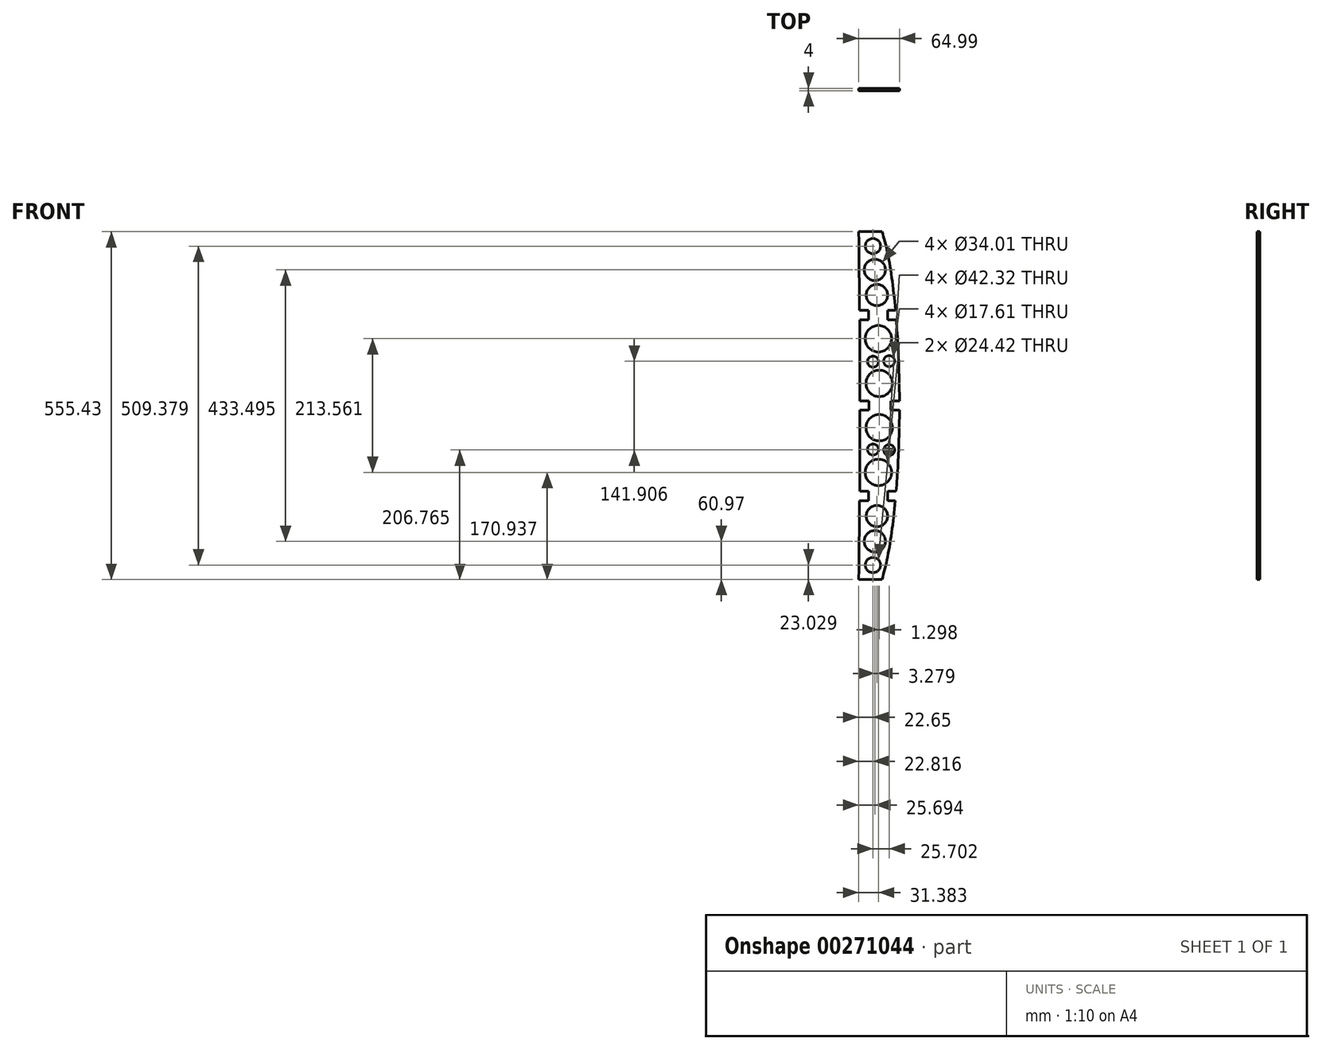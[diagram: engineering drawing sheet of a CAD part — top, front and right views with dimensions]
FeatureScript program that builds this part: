
annotation { "Feature Type Name" : "Feature", "Feature Type Description" : "" }
export const myFeature = defineFeature(function(context is Context, id is Id, definition is map)
    precondition{}
    {
        {
            var Q0;
            Q0=qCreatedBy(makeId("Front.planeOp"),FACE);
            var sketch = newSketch(context, id + "F0", { "sketchPlane" : qUnion([Q0])});
            skLineSegment(sketch, "E0", {"start": v(-136.03, -529.8) * mm, "end": v(-201.03, -530.28) * mm});
            skLineSegment(sketch, "E1", {"start": v(-201.03, -530.28) * mm, "end": v(-201.03, -252.28) * mm});
            skLineSegment(sketch, "E2", {"start": v(-201.03, -252.28) * mm, "end": v(-164.03, -252.28) * mm});
            skLineSegment(sketch, "E3.MirrorCS", {"start": v(-201.03, -530.28) * mm, "end": v(-196.95, -808.25) * mm});
            skLineSegment(sketch, "E4.MirrorCS", {"start": v(-196.95, -808.25) * mm, "end": v(-159.95, -807.7) * mm});
            skFitSpline(sketch, "E5", {"points": [v(-164.03, -252.28) * mm, v(-136.03, -529.8) * mm, v(-159.95, -807.7) * mm], "startDerivative": vector(123.85, -382.51) * mm, "endDerivative": vector(-100.33, -397.76) * mm});
            skLineSegment(sketch, "E6", {"start": v(-201.03, -530.28) * mm, "end": v(-199.03, -530.27) * mm});
            skFitSpline(sketch, "E7", {"points": [v(-201.03, -252.28) * mm, v(-199.03, -530.27) * mm, v(-196.95, -808.25) * mm], "startDerivative": vector(9.34, -915.38) * mm, "endDerivative": vector(6.18, -771.13) * mm});
            skLineSegment(sketch, "E8", {"start": v(-188.97, -530.2) * mm, "end": v(-189.03, -522.7) * mm});
            skLineSegment(sketch, "E9", {"start": v(-189.03, -522.7) * mm, "end": v(-201.03, -522.78) * mm});
            skLineSegment(sketch, "E10", {"start": v(-150.04, -529.9) * mm, "end": v(-150.04, -522.7) * mm});
            skLineSegment(sketch, "E11", {"start": v(-150.04, -522.7) * mm, "end": v(-136.04, -522.6) * mm});
            skLineSegment(sketch, "E12.MirrorCS", {"start": v(-149.94, -537.12) * mm, "end": v(-135.94, -537.02) * mm});
            skLineSegment(sketch, "E13.MirrorCS", {"start": v(-188.92, -537.7) * mm, "end": v(-200.92, -537.78) * mm});
            skLineSegment(sketch, "E14.MirrorCS", {"start": v(-150.04, -529.9) * mm, "end": v(-149.94, -537.12) * mm});
            skLineSegment(sketch, "E15.MirrorCS", {"start": v(-188.97, -530.2) * mm, "end": v(-188.92, -537.7) * mm});
            skLineSegment(sketch, "E16", {"start": v(-154.9, -385.44) * mm, "end": v(-154.9, -377.94) * mm});
            skLineSegment(sketch, "E17", {"start": v(-185.9, -377.94) * mm, "end": v(-185.9, -385.67) * mm});
            skLineSegment(sketch, "E18", {"start": v(-154.9, -377.94) * mm, "end": v(-142.05, -377.85) * mm});
            skLineSegment(sketch, "E19", {"start": v(-185.9, -377.94) * mm, "end": v(-199.9, -377.94) * mm});
            skLineSegment(sketch, "E20.MirrorCS", {"start": v(-185.78, -393.4) * mm, "end": v(-185.9, -385.67) * mm});
            skLineSegment(sketch, "E21.MirrorCS", {"start": v(-154.9, -385.44) * mm, "end": v(-154.8, -392.94) * mm});
            skLineSegment(sketch, "E22", {"start": v(-154.8, -392.94) * mm, "end": v(-140.8, -392.94) * mm});
            skLineSegment(sketch, "E23", {"start": v(-185.78, -393.4) * mm, "end": v(-199.78, -393.4) * mm});
            skCircle(sketch, "E24", {"center": v(-171.66, -493.4) * mm, "radius": 20.35 * mm});
            skCircle(sketch, "E25", {"center": v(-171.66, -424.12) * mm, "radius": 21.54 * mm});
            skCircle(sketch, "E26", {"center": v(-153.3, -459.33) * mm, "radius": 9.61 * mm});
            skCircle(sketch, "E27", {"center": v(-184.66, -459.33) * mm, "radius": 9.17 * mm});
            skCircle(sketch, "E28", {"center": v(-172.55, -350.94) * mm, "radius": 18.03 * mm});
            skCircle(sketch, "E29", {"center": v(-176.4, -308.02) * mm, "radius": 14.58 * mm});
            skCircle(sketch, "E30", {"center": v(-180.25, -272.8) * mm, "radius": 12.5 * mm});
            skCircle(sketch, "E31.MirrorC", {"center": v(-173.14, -752.16) * mm, "radius": 14.58 * mm});
            skLineSegment(sketch, "E32.MirrorCS", {"start": v(-183.77, -666.93) * mm, "end": v(-197.77, -667.14) * mm});
            skLineSegment(sketch, "E33.MirrorCS", {"start": v(-152.79, -674.43) * mm, "end": v(-152.68, -681.93) * mm});
            skCircle(sketch, "E34.MirrorC", {"center": v(-171.12, -566.74) * mm, "radius": 20.35 * mm});
            skCircle(sketch, "E35.MirrorC", {"center": v(-169.92, -709.19) * mm, "radius": 18.03 * mm});
            skLineSegment(sketch, "E36.MirrorCS", {"start": v(-152.79, -666.93) * mm, "end": v(-138.79, -666.73) * mm});
            skLineSegment(sketch, "E37.MirrorCS", {"start": v(-152.79, -674.43) * mm, "end": v(-152.79, -666.93) * mm});
            skCircle(sketch, "E38.MirrorC", {"center": v(-170.1, -636) * mm, "radius": 21.54 * mm});
            skLineSegment(sketch, "E39.MirrorCS", {"start": v(-183.77, -666.93) * mm, "end": v(-183.77, -674.66) * mm});
            skCircle(sketch, "E40.MirrorC", {"center": v(-152.26, -600.53) * mm, "radius": 9.61 * mm});
            skLineSegment(sketch, "E41.MirrorCS", {"start": v(-183.66, -682.39) * mm, "end": v(-197.66, -682.6) * mm});
            skCircle(sketch, "E42.MirrorC", {"center": v(-176.48, -787.42) * mm, "radius": 12.5 * mm});
            skLineSegment(sketch, "E43.MirrorCS", {"start": v(-183.66, -682.39) * mm, "end": v(-183.77, -674.66) * mm});
            skCircle(sketch, "E44.MirrorC", {"center": v(-183.62, -600.99) * mm, "radius": 9.17 * mm});
            skLineSegment(sketch, "E45.MirrorCS", {"start": v(-152.68, -681.93) * mm, "end": v(-139.82, -681.84) * mm});
            skLineSegment(sketch, "E46.MirrorCS", {"start": v(99.67, -703.93) * mm, "end": v(136.67, -703.93) * mm});
            skLineSegment(sketch, "E47", {"start": v(-141.4, -385.34) * mm, "end": v(-201.03, -385.78) * mm});
            skLineSegment(sketch, "E48", {"start": v(-355.28, -555.82) * mm, "end": v(-420.28, -555.82) * mm});
            skLineSegment(sketch, "E49", {"start": v(-420.28, -278.1) * mm, "end": v(-383.28, -278.1) * mm});
            skLineSegment(sketch, "E50.MirrorCS", {"start": v(-420.28, -833.54) * mm, "end": v(-383.28, -833.54) * mm});
            skLineSegment(sketch, "E51", {"start": v(-360.97, -411.32) * mm, "end": v(-420.49, -411.32) * mm});
            skLineSegment(sketch, "E52", {"start": v(-420.28, -278.1) * mm, "end": v(-420.28, -833.54) * mm});
            skLineSegment(sketch, "E53", {"start": v(-420.28, -555.82) * mm, "end": v(-418.28, -555.82) * mm});
            skFitSpline(sketch, "E54", {"points": [v(-420.28, -278.1) * mm, v(-418.28, -555.82) * mm, v(-420.28, -833.54) * mm], "startDerivative": vector(6, -555.43) * mm, "endDerivative": vector(-6.27, -554.19) * mm});
            skFitSpline(sketch, "E55", {"points": [v(-383.28, -278.1) * mm, v(-355.28, -555.82) * mm, v(-383.28, -833.54) * mm], "startDerivative": vector(107.8, -301.83) * mm, "endDerivative": vector(-107.8, -344.26) * mm});
            skLineSegment(sketch, "E56", {"start": v(-404.9, -411.32) * mm, "end": v(-404.9, -418.82) * mm});
            skLineSegment(sketch, "E57", {"start": v(-404.9, -418.82) * mm, "end": v(-418.9, -418.82) * mm});
            skLineSegment(sketch, "E58", {"start": v(-374.37, -418.82) * mm, "end": v(-374.37, -411.32) * mm});
            skLineSegment(sketch, "E59", {"start": v(-374.37, -418.82) * mm, "end": v(-360.37, -418.82) * mm});
            skLineSegment(sketch, "E60.MirrorCS", {"start": v(-404.9, -411.32) * mm, "end": v(-404.9, -403.82) * mm});
            skLineSegment(sketch, "E61.MirrorCS", {"start": v(-404.9, -403.82) * mm, "end": v(-418.9, -403.82) * mm});
            skLineSegment(sketch, "E62.MirrorCS", {"start": v(-374.37, -403.82) * mm, "end": v(-360.37, -403.82) * mm});
            skLineSegment(sketch, "E63.MirrorCS", {"start": v(-374.37, -403.82) * mm, "end": v(-374.37, -411.32) * mm});
            skCircle(sketch, "E64", {"center": v(-387.6, -520.44) * mm, "radius": 21.16 * mm});
            skCircle(sketch, "E65", {"center": v(-388.9, -449.04) * mm, "radius": 21.16 * mm});
            skCircle(sketch, "E66", {"center": v(-371.76, -484.87) * mm, "radius": 8.8 * mm});
            skCircle(sketch, "E67", {"center": v(-397.46, -485.65) * mm, "radius": 8.8 * mm});
            skCircle(sketch, "E68", {"center": v(-391.3, -379.36) * mm, "radius": 17 * mm});
            skCircle(sketch, "E69", {"center": v(-394.59, -339.07) * mm, "radius": 17 * mm});
            skCircle(sketch, "E70", {"center": v(-397.63, -301.13) * mm, "radius": 12.2 * mm});
            skLineSegment(sketch, "E71", {"start": v(-369.3, -555.82) * mm, "end": v(-369.3, -548.32) * mm});
            skLineSegment(sketch, "E72", {"start": v(-369.3, -548.32) * mm, "end": v(-355.3, -548.32) * mm});
            skLineSegment(sketch, "E73", {"start": v(-404.28, -548.32) * mm, "end": v(-404.28, -555.82) * mm});
            skLineSegment(sketch, "E74", {"start": v(-404.28, -548.32) * mm, "end": v(-418.28, -548.32) * mm});
            skLineSegment(sketch, "E75.MirrorCS", {"start": v(-369.3, -563.32) * mm, "end": v(-355.3, -563.32) * mm});
            skLineSegment(sketch, "E76.MirrorCS", {"start": v(-369.3, -555.82) * mm, "end": v(-369.3, -563.32) * mm});
            skLineSegment(sketch, "E77.MirrorCS", {"start": v(-404.28, -563.32) * mm, "end": v(-404.28, -555.82) * mm});
            skLineSegment(sketch, "E78.MirrorCS", {"start": v(-404.28, -563.32) * mm, "end": v(-418.28, -563.32) * mm});
            skCircle(sketch, "E79.MirrorC", {"center": v(-387.6, -591.2) * mm, "radius": 21.16 * mm});
            skCircle(sketch, "E80.MirrorC", {"center": v(-371.76, -626.78) * mm, "radius": 8.8 * mm});
            skCircle(sketch, "E81.MirrorC", {"center": v(-397.46, -626) * mm, "radius": 8.8 * mm});
            skCircle(sketch, "E82.MirrorC", {"center": v(-388.9, -662.6) * mm, "radius": 21.16 * mm});
            skLineSegment(sketch, "E83.MirrorCS", {"start": v(-404.9, -700.32) * mm, "end": v(-404.9, -692.82) * mm});
            skLineSegment(sketch, "E84.MirrorCS", {"start": v(-404.9, -692.82) * mm, "end": v(-418.9, -692.82) * mm});
            skLineSegment(sketch, "E85.MirrorCS", {"start": v(-374.37, -692.82) * mm, "end": v(-360.37, -692.82) * mm});
            skLineSegment(sketch, "E86.MirrorCS", {"start": v(-374.37, -707.82) * mm, "end": v(-360.37, -707.82) * mm});
            skLineSegment(sketch, "E87.MirrorCS", {"start": v(-374.37, -692.82) * mm, "end": v(-374.37, -700.32) * mm});
            skLineSegment(sketch, "E88.MirrorCS", {"start": v(-404.9, -700.32) * mm, "end": v(-404.9, -707.82) * mm});
            skLineSegment(sketch, "E89.MirrorCS", {"start": v(-360.97, -700.32) * mm, "end": v(-420.49, -700.32) * mm});
            skLineSegment(sketch, "E90.MirrorCS", {"start": v(-374.37, -707.82) * mm, "end": v(-374.37, -700.32) * mm});
            skLineSegment(sketch, "E91.MirrorCS", {"start": v(-404.9, -707.82) * mm, "end": v(-418.9, -707.82) * mm});
            skCircle(sketch, "E92.MirrorC", {"center": v(-397.63, -810.51) * mm, "radius": 12.2 * mm});
            skCircle(sketch, "E93.MirrorC", {"center": v(-394.59, -772.57) * mm, "radius": 17 * mm});
            skCircle(sketch, "E94.MirrorC", {"center": v(-391.3, -732.29) * mm, "radius": 17 * mm});
            skLineSegment(sketch, "E95", {"start": v(-418.9, -403.82) * mm, "end": v(-422.57, -403.82) * mm});
            skLineSegment(sketch, "E96", {"start": v(-418.9, -707.82) * mm, "end": v(-421.72, -707.82) * mm});
            skLineSegment(sketch, "E97", {"start": v(-418.9, -692.82) * mm, "end": v(-422.73, -692.82) * mm});
            skSolve(sketch);
        }
        {
            var Q0;
            {var subQ0=sQuery(id+"F0.wireOp",EDGE,"E56");Q0=makeQuery(id+"F0.imprint","IMPRINT",FACE,{"disambiguationData":[TD([[makeQuery(id+"F0.imprint","IMPRINT",EDGE,{"derivedFrom":subQ0}),1.0]])]});}
            var Q1;
            {var subQ13=sQuery(id+"F0.wireOp",EDGE,"E75.MirrorCS");Q1=makeQuery(id+"F0.imprint","IMPRINT",FACE,{"disambiguationData":[TD([[makeQuery(id+"F0.imprint","IMPRINT",EDGE,{"derivedFrom":subQ13}),-1.0]])]});}
            var Q2;
            {var subQ5=sQuery(id+"F0.wireOp",EDGE,"E50.MirrorCS");Q2=makeQuery(id+"F0.imprint","IMPRINT",FACE,{"disambiguationData":[TD([[makeQuery(id+"F0.imprint","IMPRINT",EDGE,{"derivedFrom":subQ5}),1.0]])]});}
            var Q3;
            {var subQ5=sQuery(id+"F0.wireOp",EDGE,"E49");Q3=makeQuery(id+"F0.imprint","IMPRINT",FACE,{"disambiguationData":[TD([[makeQuery(id+"F0.imprint","IMPRINT",EDGE,{"derivedFrom":subQ5}),-1.0]])]});}
            extrude(context, id + "F1", {"entities" : qUnion([Q0, Q1, Q2, Q3]), "depth" : 4 * mm});
        }
    });
